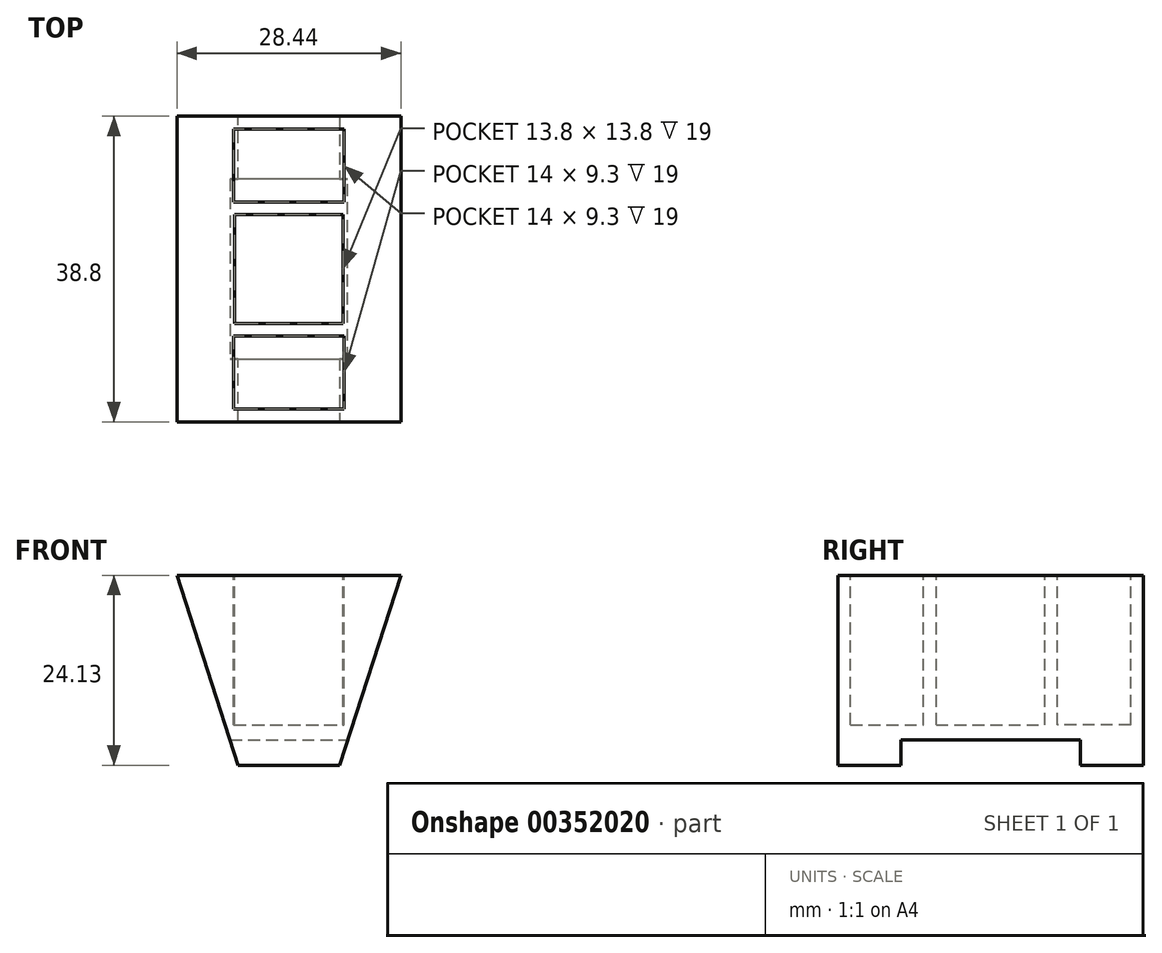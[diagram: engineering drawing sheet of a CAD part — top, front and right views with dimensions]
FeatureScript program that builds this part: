
annotation { "Feature Type Name" : "Feature", "Feature Type Description" : "" }
export const myFeature = defineFeature(function(context is Context, id is Id, definition is map)
    precondition{}
    {
        {
            var Q0;
            Q0=qCreatedBy(makeId("Top.planeOp"),FACE);
            cPlane(context, id + "F0", {"entities" : qUnion([Q0]), "cplaneType" : CPlaneType.OFFSET, "offset" : 36.12 * mm, "width" : 150 * mm, "height" : 150 * mm});
        }
        {
            var Q0;
            Q0=qCreatedBy(id+"F0.planeOp",FACE);
            var sketch = newSketch(context, id + "F1", { "sketchPlane" : qUnion([Q0])});
            skLineSegment(sketch, "E0", {"start": v(-18.1, 0) * mm, "end": v(-18.1, -38.8) * mm});
            skLineSegment(sketch, "E1", {"start": v(-18.1, -38.8) * mm, "end": v(18.1, -38.8) * mm});
            skLineSegment(sketch, "E2", {"start": v(18.1, -38.8) * mm, "end": v(18.1, 0) * mm});
            skLineSegment(sketch, "E3", {"start": v(-18.1, 0) * mm, "end": v(18.1, 0) * mm});
            skSolve(sketch);
        }
        {
            var Q0;
            Q0=qCreatedBy(makeId("Top.planeOp"),FACE);
            var sketch = newSketch(context, id + "F2", { "sketchPlane" : qUnion([Q0])});
            skLineSegment(sketch, "E4", {"start": v(6.43, 0) * mm, "end": v(6.43, -38.8) * mm});
            skLineSegment(sketch, "E5", {"start": v(6.43, -38.8) * mm, "end": v(-6.43, -38.8) * mm});
            skLineSegment(sketch, "E6", {"start": v(-6.43, -38.8) * mm, "end": v(-6.43, 0) * mm});
            skLineSegment(sketch, "E7", {"start": v(-6.43, 0) * mm, "end": v(6.43, 0) * mm});
            skSolve(sketch);
        }
        {
            var Q0;
            Q0=makeQuery(id+"F1.imprint","IMPRINT",FACE,{"disambiguationData":[TD([[makeQuery(id+"F1.imprint","IMPRINT",EDGE,{"derivedFrom":sQuery(id+"F1.wireOp",EDGE,"E0")}),1.0]])]});
            var Q1;
            Q1=makeQuery(id+"F2.imprint","IMPRINT",FACE,{"disambiguationData":[TD([[makeQuery(id+"F2.imprint","IMPRINT",EDGE,{"derivedFrom":sQuery(id+"F2.wireOp",EDGE,"E4")}),-1.0]])]});
            loft(context, id + "F3", {"sheetProfilesArray" : [{ "sheetProfileEntities" : qUnion([Q0]) }, { "sheetProfileEntities" : qUnion([Q1]) }]});
        }
        {
            var Q0;
            Q0=makeQuery(id+"F3.opLoft","CAP_FACE",FACE,{"disambiguationData":[OSD([makeQuery(id+"F1.imprint","IMPRINT",FACE,{"disambiguationData":[TD([[makeQuery(id+"F1.imprint","IMPRINT",EDGE,{"derivedFrom":sQuery(id+"F1.wireOp",EDGE,"E0")}),1.0]])]})])],"isStart":true});
            extrude(context, id + "F4", {"entities" : qUnion([Q0]), "operationType" : NewBodyOperationType.REMOVE, "oppositeDirection" : true, "depth" : 12 * mm});
        }
        {
            var Q0;
            Q0=qCreatedBy(id+"F0.planeOp",FACE);
            var sketch = newSketch(context, id + "F5", { "sketchPlane" : qUnion([Q0])});
            skLineSegment(sketch, "E8", {"start": v(-6.9, -12.5) * mm, "end": v(6.9, -12.5) * mm});
            skLineSegment(sketch, "E9", {"start": v(6.9, -12.5) * mm, "end": v(6.9, -26.3) * mm});
            skLineSegment(sketch, "E10", {"start": v(6.9, -26.3) * mm, "end": v(-6.9, -26.3) * mm});
            skLineSegment(sketch, "E11", {"start": v(-6.9, -26.3) * mm, "end": v(-6.9, -12.5) * mm});
            skSolve(sketch);
        }
        {
            var Q0;
            Q0=makeQuery(id+"F5.imprint","IMPRINT",FACE,{"disambiguationData":[TD([[makeQuery(id+"F5.imprint","IMPRINT",EDGE,{"derivedFrom":sQuery(id+"F5.wireOp",EDGE,"E8")}),-1.0]])]});
            extrude(context, id + "F6", {"entities" : qUnion([Q0]), "operationType" : NewBodyOperationType.REMOVE, "oppositeDirection" : true, "depth" : 31 * mm});
        }
        {
            var Q0;
            Q0=qCreatedBy(makeId("Top.planeOp"),FACE);
            var sketch = newSketch(context, id + "F7", { "sketchPlane" : qUnion([Q0])});
            skLineSegment(sketch, "E12", {"start": v(-10, -30.8) * mm, "end": v(10, -30.8) * mm});
            skLineSegment(sketch, "E13", {"start": v(10, -30.8) * mm, "end": v(10, -8) * mm});
            skLineSegment(sketch, "E14", {"start": v(10, -8) * mm, "end": v(-10, -8) * mm});
            skLineSegment(sketch, "E15", {"start": v(-10, -8) * mm, "end": v(-10, -30.8) * mm});
            skSolve(sketch);
        }
        {
            var Q0;
            Q0=qSketchRegion(id+"F7",true);
            extrude(context, id + "F8", {"entities" : qUnion([Q0]), "operationType" : NewBodyOperationType.REMOVE, "depth" : 3.2 * mm});
        }
        {
            var Q0;
            Q0=qCreatedBy(id+"F0.planeOp",FACE);
            var sketch = newSketch(context, id + "F9", { "sketchPlane" : qUnion([Q0])});
            skLineSegment(sketch, "E16", {"start": v(-7, -10.9) * mm, "end": v(7, -10.9) * mm});
            skLineSegment(sketch, "E17", {"start": v(7, -10.9) * mm, "end": v(7, -1.6) * mm});
            skLineSegment(sketch, "E18", {"start": v(7, -1.6) * mm, "end": v(-7, -1.6) * mm});
            skLineSegment(sketch, "E19", {"start": v(-7, -1.6) * mm, "end": v(-7, -10.9) * mm});
            skLineSegment(sketch, "E20", {"start": v(-19.21, -19.4) * mm, "end": v(16.55, -19.4) * mm, "construction": true});
            skLineSegment(sketch, "E21.MirrorCS", {"start": v(-7, -27.9) * mm, "end": v(7, -27.9) * mm});
            skLineSegment(sketch, "E22.MirrorCS", {"start": v(-7, -37.2) * mm, "end": v(-7, -27.9) * mm});
            skLineSegment(sketch, "E23.MirrorCS", {"start": v(7, -27.9) * mm, "end": v(7, -37.2) * mm});
            skLineSegment(sketch, "E24.MirrorCS", {"start": v(7, -37.2) * mm, "end": v(-7, -37.2) * mm});
            skSolve(sketch);
        }
        {
            var Q0;
            Q0 = qSketchRegion(id + "F9", true);
            extrude(context, id + "F10", {"entities" : qUnion([Q0]), "operationType" : NewBodyOperationType.REMOVE, "oppositeDirection" : true, "depth" : 31 * mm});
        }
    });
